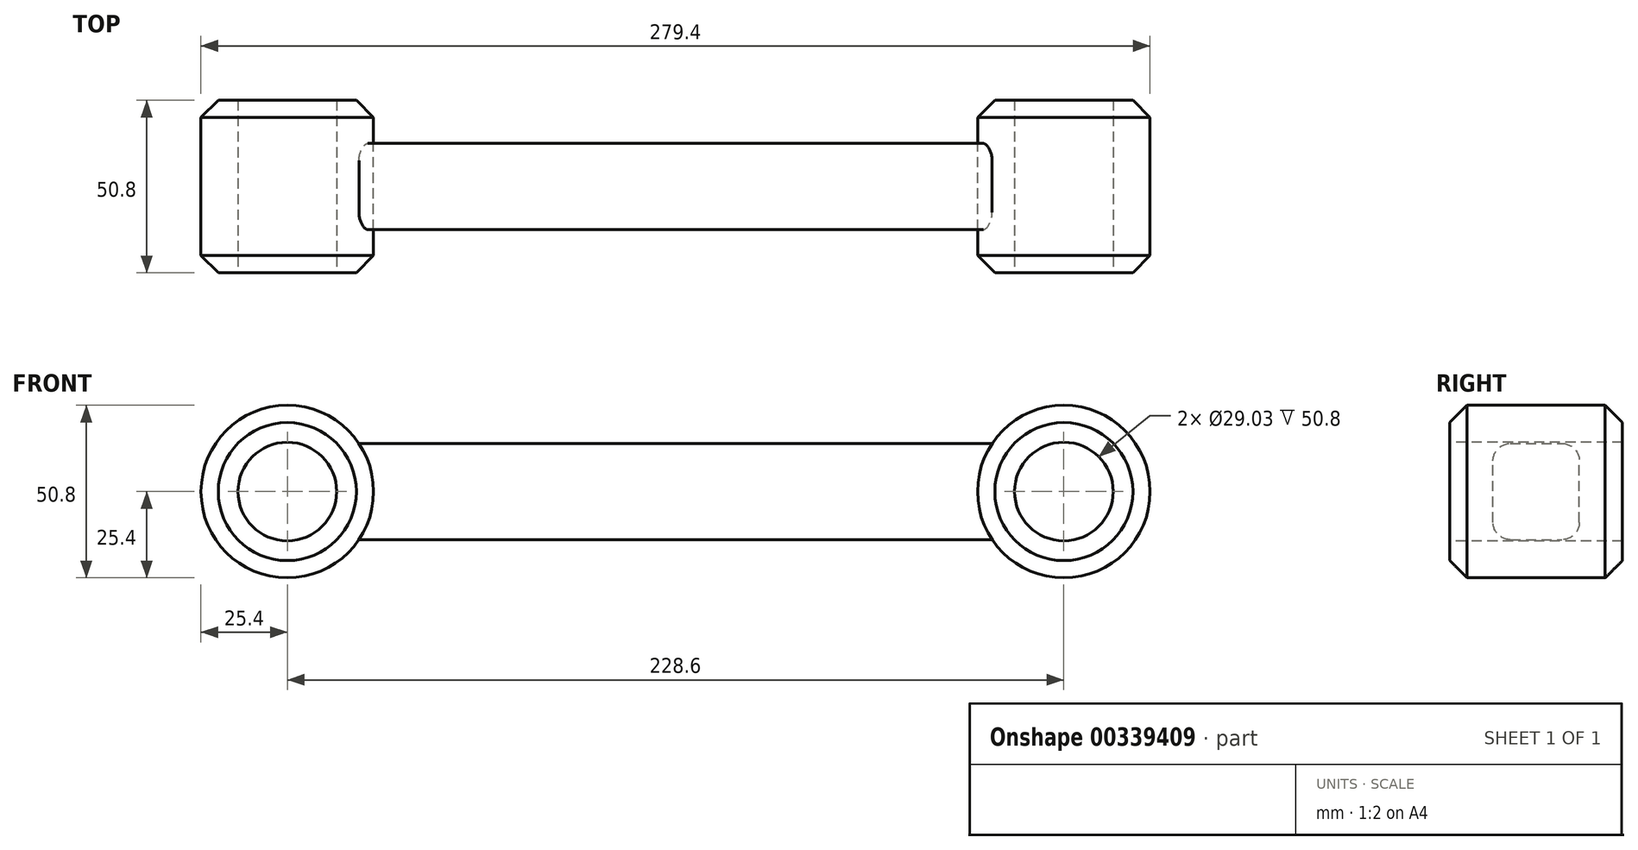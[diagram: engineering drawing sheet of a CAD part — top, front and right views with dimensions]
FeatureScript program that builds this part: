
annotation { "Feature Type Name" : "Feature", "Feature Type Description" : "" }
export const myFeature = defineFeature(function(context is Context, id is Id, definition is map)
    precondition{}
    {
        {
            var Q0;
            Q0=qCreatedBy(makeId("Front.planeOp"),FACE);
            var sketch = newSketch(context, id + "F0", { "sketchPlane" : qUnion([Q0])});
            skLineSegment(sketch, "E0.bottom", {"start": v(-114.3, -14.15) * mm, "end": v(114.3, -14.15) * mm});
            skLineSegment(sketch, "E0.top", {"start": v(-114.3, 14.15) * mm, "end": v(114.3, 14.15) * mm});
            skLineSegment(sketch, "E0.left", {"start": v(-114.3, -14.15) * mm, "end": v(-114.3, 14.15) * mm});
            skLineSegment(sketch, "E0.right", {"start": v(114.3, -14.15) * mm, "end": v(114.3, 14.15) * mm});
            skPoint(sketch, "E0.middle", {"position": v(0, 0) * mm});
            skCircle(sketch, "E1", {"center": v(-114.3, 0) * mm, "radius": 25.4 * mm});
            skCircle(sketch, "E2", {"center": v(114.3, 0) * mm, "radius": 25.4 * mm});
            skSolve(sketch);
        }
        {
            var Q0;
            {var subQ0=sQuery(id+"F0.wireOp",EDGE,"E1");var subQ1=sQuery(id+"F0.wireOp",EDGE,"E0.bottom");var subQ2=makeQuery(id+"F0.imprint","INTERSECT",VERTEX,{"derivedFrom":[subQ1,subQ0]});Q0=makeQuery(id+"F0.imprint","IMPRINT",FACE,{"disambiguationData":[TD([[makeQuery(id+"F0.imprint","IMPRINT",EDGE,{"disambiguationData":[TD([[subQ2,-1.0]])],"derivedFrom":subQ1}),1.0]])]});}
            extrude(context, id + "F1", {"entities" : qUnion([Q0]), "depth" : 12.7 * mm, "hasSecondDirection" : true, "secondDirectionOppositeDirection" : true, "secondDirectionDepth" : 12.7 * mm});
        }
        {
            var Q0;
            {var subQ0=sQuery(id+"F0.wireOp",EDGE,"E0.left");Q0=makeQuery(id+"F0.imprint","IMPRINT",FACE,{"disambiguationData":[TD([[makeQuery(id+"F0.imprint","IMPRINT",EDGE,{"derivedFrom":subQ0}),1.0]])]});}
            var Q1;
            {var subQ0=sQuery(id+"F0.wireOp",EDGE,"E0.left");Q1=makeQuery(id+"F0.imprint","IMPRINT",FACE,{"disambiguationData":[TD([[makeQuery(id+"F0.imprint","IMPRINT",EDGE,{"derivedFrom":subQ0}),-1.0]])]});}
            extrude(context, id + "F2", {"entities" : qUnion([Q0, Q1]), "depth" : 25.4 * mm, "hasSecondDirection" : true, "secondDirectionOppositeDirection" : true, "secondDirectionDepth" : 25.4 * mm});
        }
        {
            var Q0;
            {var subQ0=sQuery(id+"F0.wireOp",EDGE,"E0.right");Q0=makeQuery(id+"F0.imprint","IMPRINT",FACE,{"disambiguationData":[TD([[makeQuery(id+"F0.imprint","IMPRINT",EDGE,{"derivedFrom":subQ0}),-1.0]])]});}
            var Q1;
            {var subQ0=sQuery(id+"F0.wireOp",EDGE,"E0.right");Q1=makeQuery(id+"F0.imprint","IMPRINT",FACE,{"disambiguationData":[TD([[makeQuery(id+"F0.imprint","IMPRINT",EDGE,{"derivedFrom":subQ0}),1.0]])]});}
            extrude(context, id + "F3", {"entities" : qUnion([Q0, Q1]), "depth" : 25.4 * mm, "hasSecondDirection" : true, "secondDirectionOppositeDirection" : true, "secondDirectionDepth" : 25.4 * mm});
        }
        {
            var Q0;
            Q0=makeQuery(id+"F2.opExtrude","CAP_FACE",FACE,{"disambiguationData":[OSD([sQuery(id+"F0.wireOp",EDGE,"E1")])],"isStart":false});
            var sketch = newSketch(context, id + "F4", { "sketchPlane" : qUnion([Q0])});
            skCircle(sketch, "E3", {"center": v(-114.3, 0) * mm, "radius": 14.52 * mm});
            skSolve(sketch);
        }
        {
            var Q0;
            Q0=makeQuery(id+"F4.imprint","IMPRINT",FACE,{"disambiguationData":[TD([[makeQuery(id+"F4.imprint","IMPRINT",EDGE,{"derivedFrom":sQuery(id+"F4.wireOp",EDGE,"E3")}),1.0]])]});
            extrude(context, id + "F5", {"entities" : qUnion([Q0]), "operationType" : NewBodyOperationType.REMOVE, "endBound" : BoundingType.THROUGH_ALL, "oppositeDirection" : true, "depth" : 25.4 * mm});
        }
        {
            var Q0;
            Q0=makeQuery(id+"F3.opExtrude","CAP_FACE",FACE,{"disambiguationData":[OSD([sQuery(id+"F0.wireOp",EDGE,"E2")])],"isStart":false});
            var sketch = newSketch(context, id + "F6", { "sketchPlane" : qUnion([Q0])});
            skCircle(sketch, "E4", {"center": v(114.3, 0) * mm, "radius": 14.52 * mm});
            skSolve(sketch);
        }
        {
            var Q0;
            Q0=makeQuery(id+"F6.imprint","IMPRINT",FACE,{"disambiguationData":[TD([[makeQuery(id+"F6.imprint","IMPRINT",EDGE,{"derivedFrom":sQuery(id+"F6.wireOp",EDGE,"E4")}),1.0]])]});
            extrude(context, id + "F7", {"entities" : qUnion([Q0]), "operationType" : NewBodyOperationType.REMOVE, "endBound" : BoundingType.THROUGH_ALL, "oppositeDirection" : true, "depth" : 25.4 * mm});
        }
        {
            var Q0;
            Q0=makeQuery(id+"F2.opExtrude","CAP_EDGE",EDGE,{"disambiguationData":[OSD([sQuery(id+"F0.wireOp",EDGE,"E1")])],"isStart":false});
            var Q1;
            Q1=makeQuery(id+"F2.opExtrude","CAP_EDGE",EDGE,{"disambiguationData":[OSD([sQuery(id+"F0.wireOp",EDGE,"E1")])],"isStart":true});
            var Q2;
            Q2=makeQuery(id+"F3.opExtrude","CAP_EDGE",EDGE,{"disambiguationData":[OSD([sQuery(id+"F0.wireOp",EDGE,"E2")])],"isStart":false});
            var Q3;
            Q3=makeQuery(id+"F3.opExtrude","CAP_EDGE",EDGE,{"disambiguationData":[OSD([sQuery(id+"F0.wireOp",EDGE,"E2")])],"isStart":true});
            chamfer(context, id + "F8", {"entities" : qUnion([Q0, Q1, Q2, Q3]), "width" : 5.08 * mm, "tangentPropagation" : true});
        }
        {
            var Q0;
            Q0=makeQuery(id+"F1.opExtrude","CAP_EDGE",EDGE,{"disambiguationData":[OSD([sQuery(id+"F0.wireOp",EDGE,"E0.top")])],"isStart":false});
            var Q1;
            Q1=makeQuery(id+"F1.opExtrude","CAP_EDGE",EDGE,{"disambiguationData":[OSD([sQuery(id+"F0.wireOp",EDGE,"E0.top")])],"isStart":true});
            var Q2;
            Q2=makeQuery(id+"F1.opExtrude","CAP_EDGE",EDGE,{"disambiguationData":[OSD([sQuery(id+"F0.wireOp",EDGE,"E0.bottom")])],"isStart":false});
            var Q3;
            Q3=makeQuery(id+"F1.opExtrude","CAP_EDGE",EDGE,{"disambiguationData":[OSD([sQuery(id+"F0.wireOp",EDGE,"E0.bottom")])],"isStart":true});
            fillet(context, id + "F9", {"entities" : qUnion([Q0, Q1, Q2, Q3]), "radius" : 5.08 * mm, "tangentPropagation" : true, "allowEdgeOverflow" : false});
        }
    });
